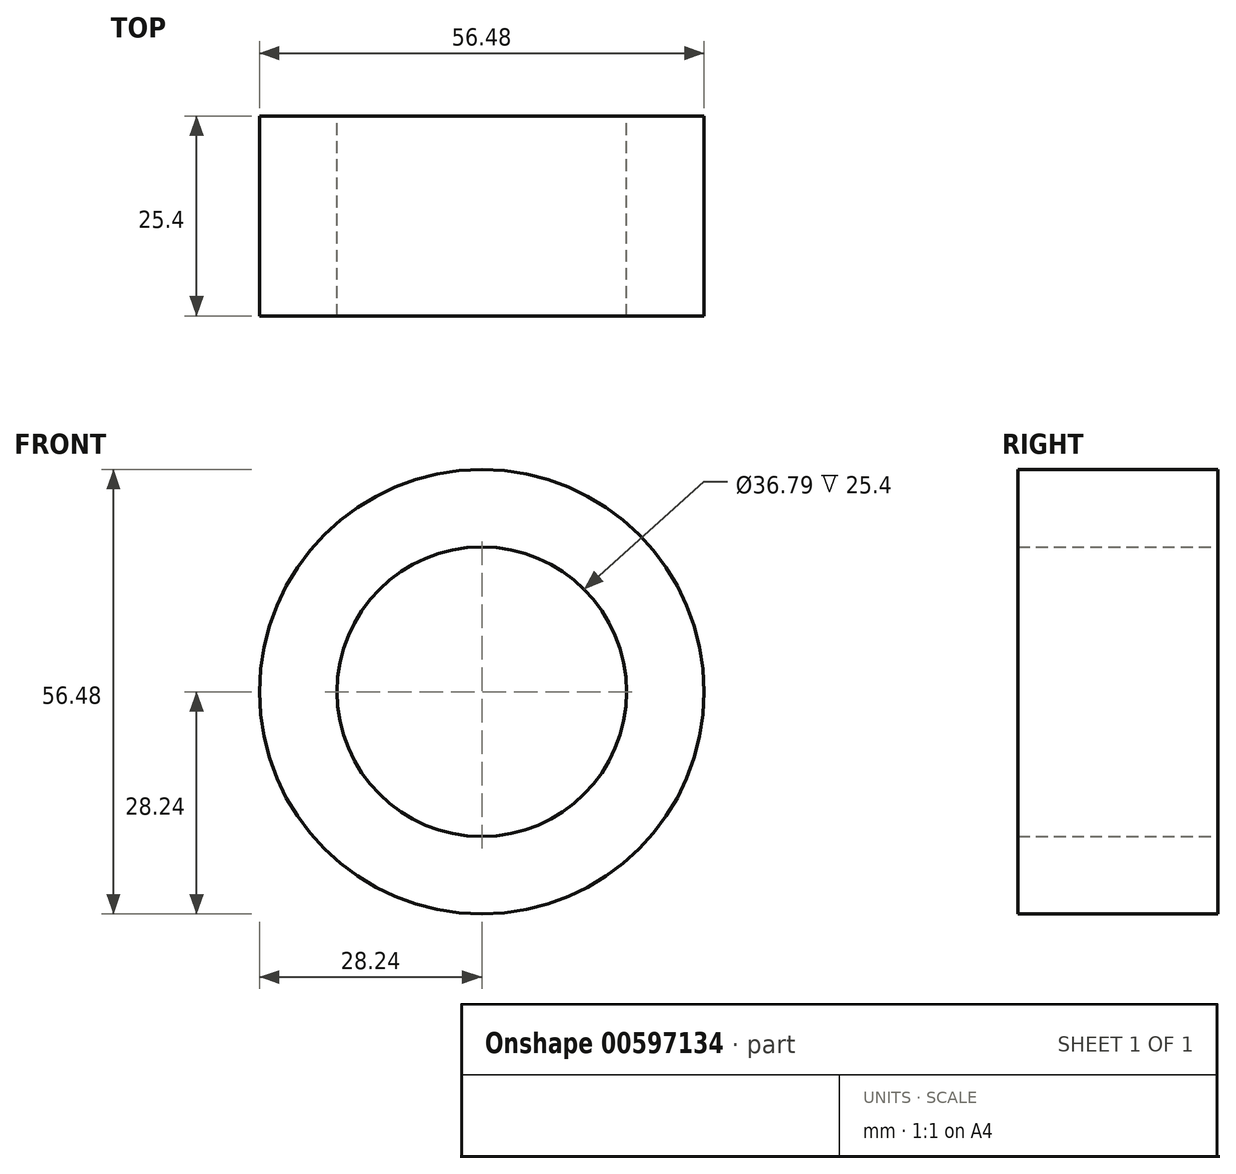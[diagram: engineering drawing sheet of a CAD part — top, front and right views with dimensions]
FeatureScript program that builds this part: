
annotation { "Feature Type Name" : "Feature", "Feature Type Description" : "" }
export const myFeature = defineFeature(function(context is Context, id is Id, definition is map)
    precondition{}
    {
        {
            var Q0;
            Q0=qCreatedBy(makeId("Front.planeOp"),FACE);
            var sketch = newSketch(context, id + "F0", { "sketchPlane" : qUnion([Q0])});
            skCircle(sketch, "E0", {"center": v(0, 0) * mm, "radius": 28.24 * mm});
            skCircle(sketch, "E1", {"center": v(0, 0) * mm, "radius": 18.4 * mm});
            skCircle(sketch, "E2", {"center": v(0, 0) * mm, "radius": 76.52 * mm});
            skSolve(sketch);
        }
        {
            var Q0;
            Q0=makeQuery(id+"F0.imprint","IMPRINT",FACE,{"disambiguationData":[TD([[makeQuery(id+"F0.imprint","IMPRINT",EDGE,{"derivedFrom":sQuery(id+"F0.wireOp",EDGE,"E0")}),1.0]])]});
            extrude(context, id + "F1", {"entities" : qUnion([Q0]), "depth" : 25.4 * mm, "offsetDistance" : 25.4 * mm});
        }
    });
